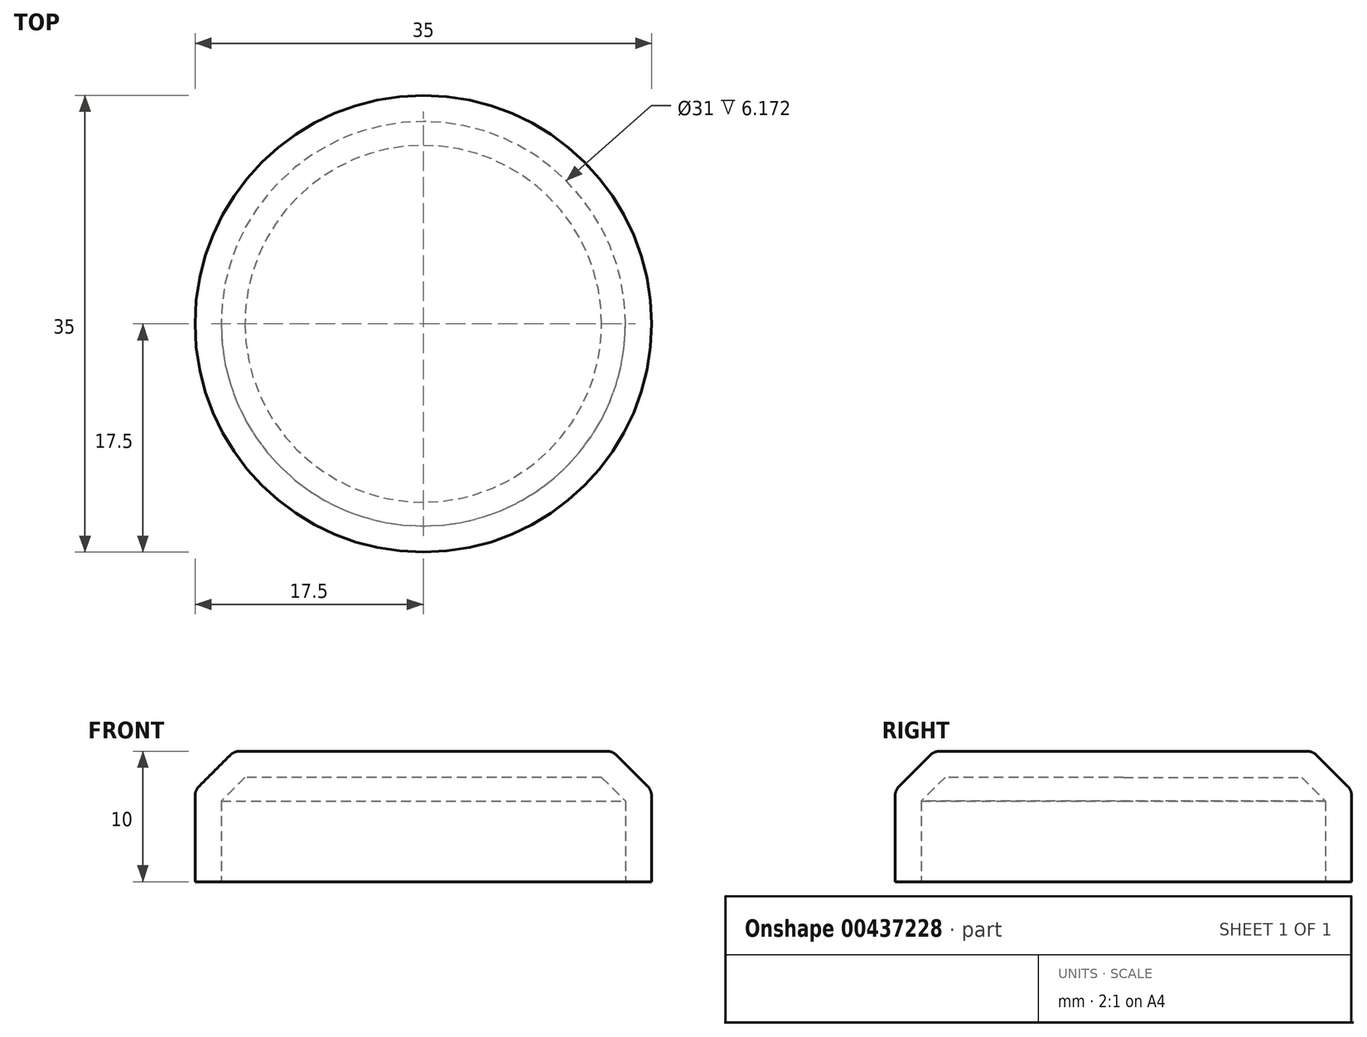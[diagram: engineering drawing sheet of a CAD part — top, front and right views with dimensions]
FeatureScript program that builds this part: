
annotation { "Feature Type Name" : "Feature", "Feature Type Description" : "" }
export const myFeature = defineFeature(function(context is Context, id is Id, definition is map)
    precondition{}
    {
        {
            var Q0;
            Q0=qCreatedBy(makeId("Top.planeOp"),FACE);
            var sketch = newSketch(context, id + "F0", { "sketchPlane" : qUnion([Q0])});
            skCircle(sketch, "E0", {"center": v(0, 0) * mm, "radius": 17.5 * mm});
            skSolve(sketch);
        }
        {
            var Q0;
            Q0=makeQuery(id+"F0.imprint","IMPRINT",FACE,{"disambiguationData":[TD([[makeQuery(id+"F0.imprint","IMPRINT",EDGE,{"derivedFrom":sQuery(id+"F0.wireOp",EDGE,"E0")}),1.0]])]});
            extrude(context, id + "F1", {"entities" : qUnion([Q0]), "depth" : 10 * mm});
        }
        {
            var Q0;
            Q0=makeQuery(id+"F1.opExtrude","CAP_EDGE",EDGE,{"disambiguationData":[OSD([sQuery(id+"F0.wireOp",EDGE,"E0")])],"isStart":false});
            chamfer(context, id + "F2", {"entities" : qUnion([Q0]), "width" : 3 * mm, "tangentPropagation" : true});
        }
        {
            var Q0;
            Q0=makeQuery(id+"F2.opChamfer","BLEND_FACE",FACE,{"disambiguationData":[OSD([sQuery(id+"F0.wireOp",EDGE,"E0")])]});
            fillet(context, id + "F3", {"entities" : qUnion([Q0]), "radius" : 1 * mm, "tangentPropagation" : true, "allowEdgeOverflow" : false});
        }
        {
            var Q0;
            Q0=makeQuery(id+"F1.opExtrude","CAP_FACE",FACE,{"disambiguationData":[OSD([sQuery(id+"F0.wireOp",EDGE,"E0")])],"isStart":true});
            shell(context, id + "F4", {"entities" : qUnion([Q0]), "thickness" : 2 * mm});
        }
    });
